# Revit family: Shower-Valve_Trim-KOHLER-Composed-K-T73133BR_1
name_source: partatom
category: Specialty Equipment
revit_build: Autodesk Revit 2017 (Build: 20160225_1515(x64)
units: mm (PartAtom-declared; Revit-internal decimal feet)

## family parameters
Cut with Voids When Loaded = No
Host = Face
OmniClass Number = 23.31.25.00
OmniClass Title = Toilet and Bath Specialties
Part Type = Normal
Room Calculation Point = No
Round Connector Dimension = Use Diameter
Shared = No

## types (4) — shared parameters
ADA Compliant = Yes
Assembly Code = C1030200
Date Modified = 05/25/2021
Default Elevation = 42"
Description = THERMOSTATIC VALVE TRIM
Height = 6 3/8"
Length = 3 5/16"
Manufacturer = KOHLER Co.
Master Format 2014 = 10 28 00
Master Format 2014 Name = Toilet, Bath, and Laundry Accessories
Material = Premium Metal Construction
Product Name = COMPOSED
Product Page URL = https://br.kohler.com
URL = https://br.kohler.com
WaterSense Certified = No
Width = 6 3/8"

## per-type parameters (varying)
| type | Cross Handle | Dist | Finish | Handle Clearance | Lever Handle | Model | Type |
| Lever Handle, TT-Vibrant Titanium | No | 0" | Kohler-Metal-TT-Vibrant_Titanium | 3 1/4" | Yes | K-T73133BR-4-TT | 1 |
| Cross Handle, TT-Vibrant Titanium | Yes | 1 1/2" | Kohler-Metal-TT-Vibrant_Titanium | 3" | No | K-T73133BR-3-TT | 2 |
| Lever Handle, CP-Polished Chrome | No | 0" | Kohler-Metal-CP-Polished_Chrome | 3 1/4" | Yes | K-T73133BR-4-CP | 3 |
| Lever Handle, BL-Matte Black | No | 0" | Kohler-Metal-BL-Matte_Black | 3 1/4" | Yes | K-T73133BR-4-BL | 4 |

## geometry (parser evidence)
native form markers: Sweep x6
no freeform markers — native parametric forms only
